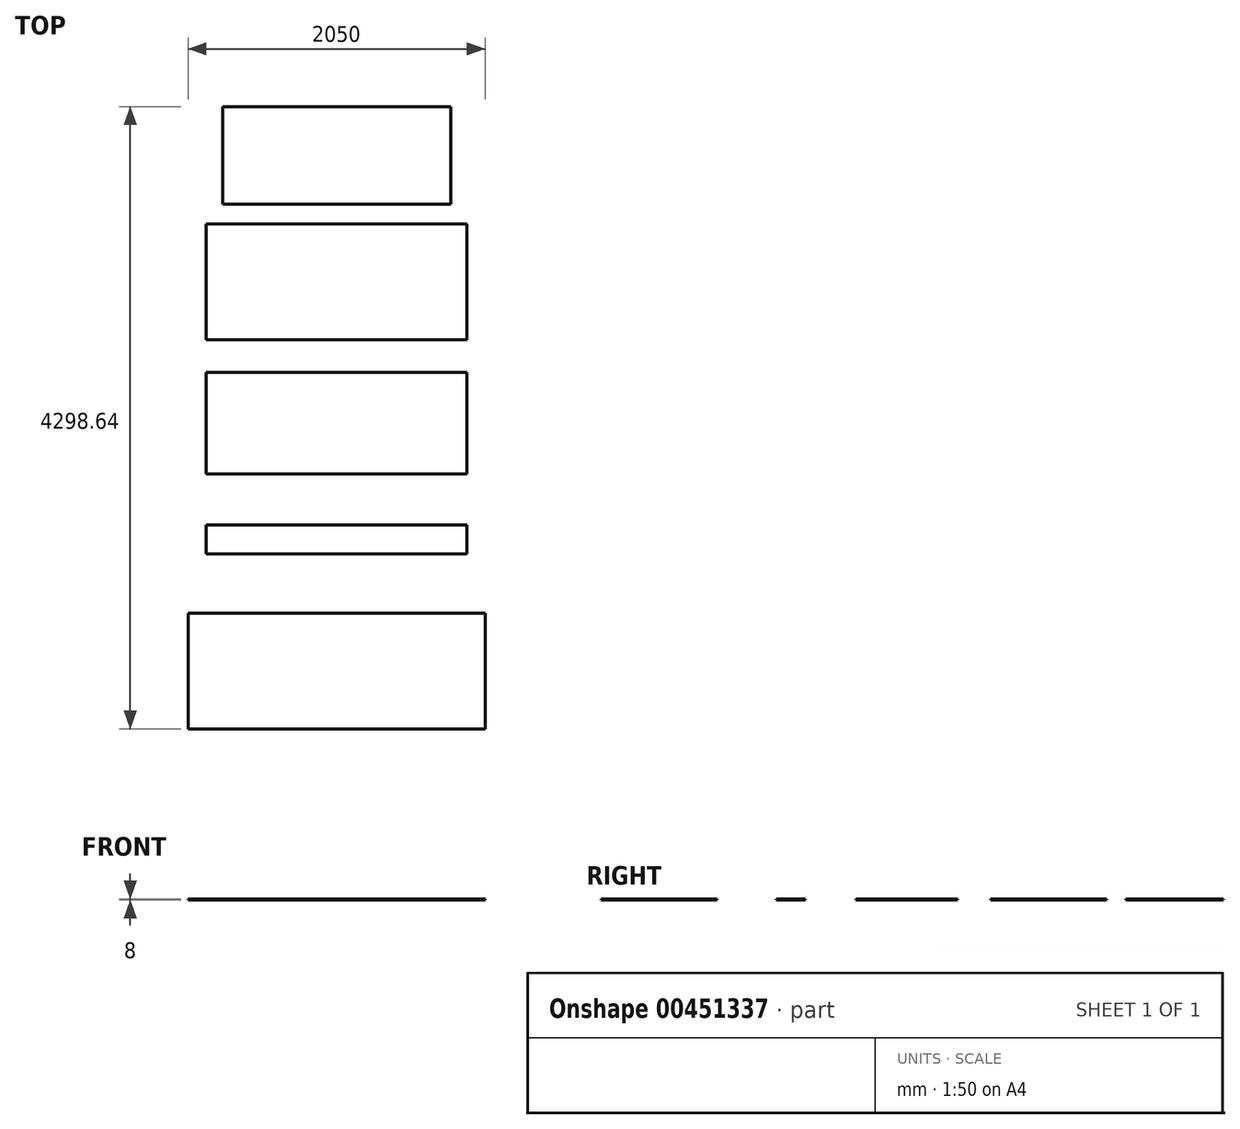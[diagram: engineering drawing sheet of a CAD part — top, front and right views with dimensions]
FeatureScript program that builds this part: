
annotation { "Feature Type Name" : "Feature", "Feature Type Description" : "" }
export const myFeature = defineFeature(function(context is Context, id is Id, definition is map)
    precondition{}
    {
        {
            var Q0;
            Q0=qCreatedBy(makeId("Top.planeOp"),FACE);
            var sketch = newSketch(context, id + "F0", { "sketchPlane" : qUnion([Q0])});
            skLineSegment(sketch, "E0.bottom", {"start": v(900, 400) * mm, "end": v(-900, 400) * mm});
            skLineSegment(sketch, "E0.top", {"start": v(900, -400) * mm, "end": v(-900, -400) * mm});
            skLineSegment(sketch, "E0.left", {"start": v(900, 400) * mm, "end": v(900, -400) * mm});
            skLineSegment(sketch, "E0.right", {"start": v(-900, 400) * mm, "end": v(-900, -400) * mm});
            skPoint(sketch, "E0.middle", {"position": v(0, 0) * mm});
            skLineSegment(sketch, "E1.bottom", {"start": v(788, 1209.45) * mm, "end": v(-788, 1209.45) * mm});
            skLineSegment(sketch, "E1.top", {"start": v(788, 535.45) * mm, "end": v(-788, 535.45) * mm});
            skLineSegment(sketch, "E1.left", {"start": v(788, 1209.45) * mm, "end": v(788, 535.45) * mm});
            skLineSegment(sketch, "E1.right", {"start": v(-788, 1209.45) * mm, "end": v(-788, 535.45) * mm});
            skPoint(sketch, "E1.middle", {"position": v(0, 872.45) * mm});
            skLineSegment(sketch, "E2.bottom", {"start": v(900, -627.34) * mm, "end": v(-900, -627.34) * mm});
            skLineSegment(sketch, "E2.top", {"start": v(900, -1327.34) * mm, "end": v(-900, -1327.34) * mm});
            skLineSegment(sketch, "E2.left", {"start": v(900, -627.34) * mm, "end": v(900, -1327.34) * mm});
            skLineSegment(sketch, "E2.right", {"start": v(-900, -627.34) * mm, "end": v(-900, -1327.34) * mm});
            skPoint(sketch, "E2.middle", {"position": v(0, -977.34) * mm});
            skPoint(sketch, "E2.middle.positionSnap0", {"position": v(0, -400) * mm});
            skPoint(sketch, "E2.centerSnap0", {"position": v(0, -400) * mm});
            skLineSegment(sketch, "E3.bottom", {"start": v(900, -1679.43) * mm, "end": v(-900, -1679.43) * mm});
            skLineSegment(sketch, "E3.top", {"start": v(900, -1879.43) * mm, "end": v(-900, -1879.43) * mm});
            skLineSegment(sketch, "E3.left", {"start": v(900, -1679.43) * mm, "end": v(900, -1879.43) * mm});
            skLineSegment(sketch, "E3.right", {"start": v(-900, -1679.43) * mm, "end": v(-900, -1879.43) * mm});
            skPoint(sketch, "E3.middle", {"position": v(0, -1779.43) * mm});
            skLineSegment(sketch, "E4.bottom", {"start": v(1025, -2289.2) * mm, "end": v(-1025, -2289.2) * mm});
            skLineSegment(sketch, "E4.top", {"start": v(1025, -3089.2) * mm, "end": v(-1025, -3089.2) * mm});
            skLineSegment(sketch, "E4.left", {"start": v(1025, -2289.2) * mm, "end": v(1025, -3089.2) * mm});
            skLineSegment(sketch, "E4.right", {"start": v(-1025, -2289.2) * mm, "end": v(-1025, -3089.2) * mm});
            skPoint(sketch, "E4.middle", {"position": v(0, -2689.2) * mm});
            skPoint(sketch, "E4.middle.positionSnap0", {"position": v(0, -1879.43) * mm});
            skPoint(sketch, "E4.centerSnap0", {"position": v(0, -1879.43) * mm});
            skSolve(sketch);
        }
        {
            var Q0;
            Q0 = qSketchRegion(id + "F0", true);
            extrude(context, id + "F1", {"entities" : qUnion([Q0]), "depth" : 8 * mm});
        }
    });
